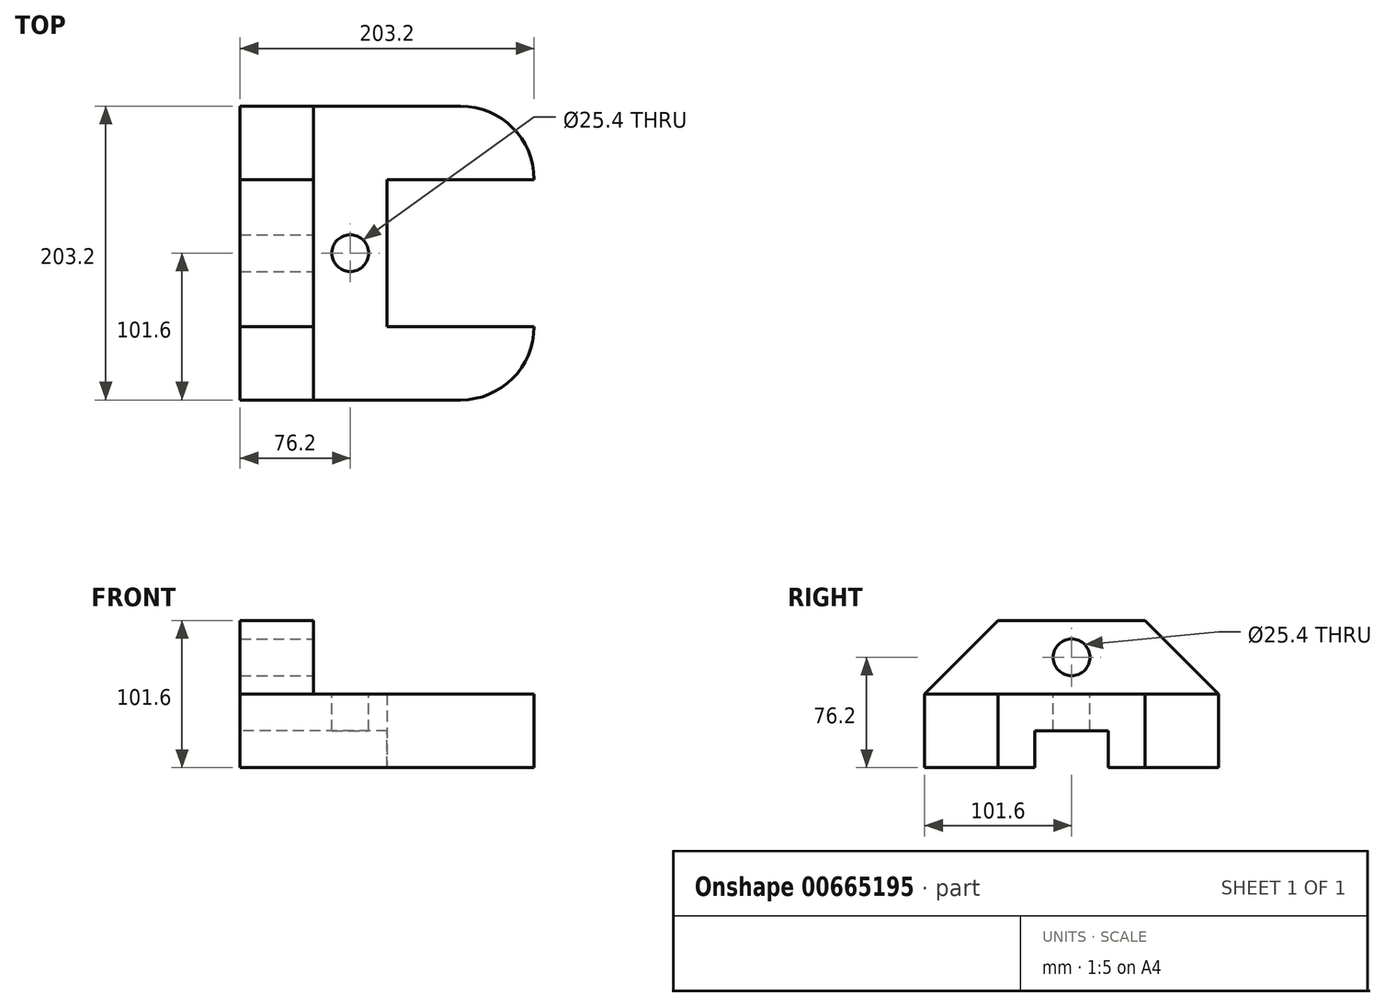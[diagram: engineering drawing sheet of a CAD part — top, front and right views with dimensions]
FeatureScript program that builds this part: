
annotation { "Feature Type Name" : "Feature", "Feature Type Description" : "" }
export const myFeature = defineFeature(function(context is Context, id is Id, definition is map)
    precondition{}
    {
        {
            var Q0;
            Q0=qCreatedBy(makeId("Front.planeOp"),FACE);
            var sketch = newSketch(context, id + "F0", { "sketchPlane" : qUnion([Q0])});
            skLineSegment(sketch, "E0", {"start": v(0, 0) * mm, "end": v(0, 76.2) * mm});
            skLineSegment(sketch, "E1", {"start": v(0, 76.2) * mm, "end": v(50.8, 76.2) * mm});
            skLineSegment(sketch, "E2", {"start": v(50.8, 76.2) * mm, "end": v(50.8, 25.4) * mm});
            skLineSegment(sketch, "E3", {"start": v(50.8, 25.4) * mm, "end": v(101.6, 25.4) * mm});
            skLineSegment(sketch, "E4", {"start": v(101.6, 25.4) * mm, "end": v(101.6, 0) * mm});
            skLineSegment(sketch, "E5", {"start": v(101.6, 0) * mm, "end": v(0, 0) * mm});
            skLineSegment(sketch, "E6", {"start": v(0, 0) * mm, "end": v(0, -25.4) * mm});
            skLineSegment(sketch, "E7", {"start": v(0, -25.4) * mm, "end": v(101.6, -25.4) * mm});
            skLineSegment(sketch, "E8", {"start": v(101.6, -25.4) * mm, "end": v(101.6, 0) * mm});
            skSolve(sketch);
        }
        {
            var Q0;
            Q0=makeQuery(id+"F0.imprint","IMPRINT",FACE,{"disambiguationData":[TD([[makeQuery(id+"F0.imprint","IMPRINT",EDGE,{"derivedFrom":sQuery(id+"F0.wireOp",EDGE,"E0")}),-1.0]])]});
            extrude(context, id + "F1", {"entities" : qUnion([Q0]), "endBound" : BoundingType.SYMMETRIC, "depth" : 101.6 * mm, "offsetDistance" : 25.4 * mm});
        }
        {
            var Q0;
            Q0=makeQuery(id+"F1.opExtrude","SWEPT_FACE",FACE,{"disambiguationData":[OSD([sQuery(id+"F0.wireOp",EDGE,"E5")])]});
            var sketch = newSketch(context, id + "F2", { "sketchPlane" : qUnion([Q0])});
            skLineSegment(sketch, "E9", {"start": v(101.6, 25.4) * mm, "end": v(0, 25.4) * mm});
            skLineSegment(sketch, "E10", {"start": v(101.6, -25.4) * mm, "end": v(0, -25.4) * mm});
            skSolve(sketch);
        }
        {
            var Q0;
            {var subQ0=sQuery(id+"F2.wireOp",EDGE,"E9");Q0=makeQuery(id+"F2.imprint","IMPRINT",FACE,{"disambiguationData":[TD([[makeQuery(id+"F2.imprint","IMPRINT",EDGE,{"derivedFrom":subQ0}),-1.0]])]});}
            var Q1;
            {var subQ0=sQuery(id+"F2.wireOp",EDGE,"E10");Q1=makeQuery(id+"F2.imprint","IMPRINT",FACE,{"disambiguationData":[TD([[makeQuery(id+"F2.imprint","IMPRINT",EDGE,{"derivedFrom":subQ0}),1.0]])]});}
            extrude(context, id + "F3", {"entities" : qUnion([Q0, Q1]), "operationType" : NewBodyOperationType.ADD, "depth" : 25.4 * mm, "offsetDistance" : 25.4 * mm});
        }
        {
            var Q0;
            {var subQ0=sQuery(id+"F0.wireOp",EDGE,"E5");var subQ1=sQuery(id+"F0.wireOp",EDGE,"E6");var subQ2=sQuery(id+"F0.wireOp",EDGE,"E0");var subQ3=makeQuery(id+"F1.opExtrude","SWEPT_EDGE",EDGE,{"disambiguationData":[OSD([subQ2,subQ0,subQ1])]});Q0=makeQuery(id+"F3.boolean.opBoolean","MERGE",FACE,{"derivedFrom":[makeQuery(id+"F1.opExtrude","SWEPT_FACE",FACE,{"disambiguationData":[OSD([subQ2])]}),makeQuery(id+"F3.opExtrude","SWEPT_FACE",FACE,{"disambiguationData":[OSD([subQ2,subQ0,subQ1]),TDD([makeQuery(id+"F2.imprint","IMPRINT",EDGE,{"disambiguationData":[TD([[makeQuery(id+"F2.imprint","INTERSECT",VERTEX,{"derivedFrom":[subQ3,makeQuery(id+"F1.opExtrude","CAP_EDGE",EDGE,{"disambiguationData":[OSD([subQ0])],"isStart":true})]}),1.0]])],"derivedFrom":subQ3})])]}),makeQuery(id+"F3.opExtrude","SWEPT_FACE",FACE,{"disambiguationData":[OSD([subQ2,subQ0,subQ1]),TDD([makeQuery(id+"F2.imprint","IMPRINT",EDGE,{"disambiguationData":[TD([[makeQuery(id+"F2.imprint","INTERSECT",VERTEX,{"derivedFrom":[subQ3,makeQuery(id+"F1.opExtrude","CAP_EDGE",EDGE,{"disambiguationData":[OSD([subQ0])],"isStart":false})]}),-1.0]])],"derivedFrom":subQ3})])]})]});}
            var sketch = newSketch(context, id + "F4", { "sketchPlane" : qUnion([Q0])});
            skLineSegment(sketch, "E11", {"start": v(-50.8, -25.4) * mm, "end": v(-101.6, -25.4) * mm});
            skLineSegment(sketch, "E12", {"start": v(-101.6, -25.4) * mm, "end": v(-101.6, 25.4) * mm});
            skLineSegment(sketch, "E13", {"start": v(-101.6, 25.4) * mm, "end": v(-50.8, 25.4) * mm});
            skLineSegment(sketch, "E14", {"start": v(50.8, -25.4) * mm, "end": v(101.6, -25.4) * mm});
            skLineSegment(sketch, "E15", {"start": v(101.6, -25.4) * mm, "end": v(101.6, 25.4) * mm});
            skLineSegment(sketch, "E16", {"start": v(101.6, 25.4) * mm, "end": v(50.8, 25.4) * mm});
            skLineSegment(sketch, "E17", {"start": v(-50.8, 76.2) * mm, "end": v(-101.6, 25.4) * mm});
            skLineSegment(sketch, "E18", {"start": v(50.8, 76.2) * mm, "end": v(101.6, 25.4) * mm});
            skSolve(sketch);
        }
        {
            var Q0;
            {var subQ0=sQuery(id+"F4.wireOp",EDGE,"E16");Q0=makeQuery(id+"F4.imprint","IMPRINT",FACE,{"disambiguationData":[TD([[makeQuery(id+"F4.imprint","IMPRINT",EDGE,{"derivedFrom":subQ0}),-1.0]])]});}
            var Q1;
            {var subQ0=sQuery(id+"F4.wireOp",EDGE,"E13");Q1=makeQuery(id+"F4.imprint","IMPRINT",FACE,{"disambiguationData":[TD([[makeQuery(id+"F4.imprint","IMPRINT",EDGE,{"derivedFrom":subQ0}),1.0]])]});}
            extrude(context, id + "F5", {"entities" : qUnion([Q0, Q1]), "operationType" : NewBodyOperationType.ADD, "oppositeDirection" : true, "depth" : 50.8 * mm, "offsetDistance" : 25.4 * mm});
        }
        {
            var Q0;
            {var subQ0=sQuery(id+"F4.wireOp",EDGE,"E11");Q0=makeQuery(id+"F4.imprint","IMPRINT",FACE,{"disambiguationData":[TD([[makeQuery(id+"F4.imprint","IMPRINT",EDGE,{"derivedFrom":subQ0}),-1.0]])]});}
            var Q1;
            {var subQ0=sQuery(id+"F4.wireOp",EDGE,"E14");Q1=makeQuery(id+"F4.imprint","IMPRINT",FACE,{"disambiguationData":[TD([[makeQuery(id+"F4.imprint","IMPRINT",EDGE,{"derivedFrom":subQ0}),1.0]])]});}
            extrude(context, id + "F6", {"entities" : qUnion([Q0, Q1]), "operationType" : NewBodyOperationType.ADD, "oppositeDirection" : true, "depth" : 203.2 * mm, "offsetDistance" : 25.4 * mm});
        }
        {
            var Q0;
            Q0=makeQuery(id+"F6.opExtrude","CAP_EDGE",EDGE,{"disambiguationData":[OSD([sQuery(id+"F4.wireOp",EDGE,"E15")])],"isStart":false});
            var Q1;
            Q1=makeQuery(id+"F6.opExtrude","CAP_EDGE",EDGE,{"disambiguationData":[OSD([sQuery(id+"F4.wireOp",EDGE,"E12")])],"isStart":false});
            fillet(context, id + "F7", {"entities" : qUnion([Q0, Q1]), "radius" : 50.8 * mm, "tangentPropagation" : true, "allowEdgeOverflow" : false});
        }
        {
            var Q0;
            Q0=makeQuery(id+"F6.boolean.opBoolean","MERGE",FACE,{"derivedFrom":[makeQuery(id+"F1.opExtrude","SWEPT_FACE",FACE,{"disambiguationData":[OSD([sQuery(id+"F0.wireOp",EDGE,"E3")])]}),makeQuery(id+"F6.opExtrude","SWEPT_FACE",FACE,{"disambiguationData":[OSD([sQuery(id+"F4.wireOp",EDGE,"E13")])]}),makeQuery(id+"F6.opExtrude","SWEPT_FACE",FACE,{"disambiguationData":[OSD([sQuery(id+"F4.wireOp",EDGE,"E16")])]})]});
            var sketch = newSketch(context, id + "F8", { "sketchPlane" : qUnion([Q0])});
            skPoint(sketch, "E19", {"position": v(76.2, 0) * mm});
            skSolve(sketch);
        }
        {
            var Q0;
            {var subQ0=sQuery(id+"F0.wireOp",EDGE,"E6");var subQ1=sQuery(id+"F0.wireOp",EDGE,"E5");var subQ2=sQuery(id+"F0.wireOp",EDGE,"E0");Q0=makeQuery(id+"F5.boolean.opBoolean","MERGE",FACE,{"derivedFrom":[makeQuery(id+"F1.opExtrude","SWEPT_FACE",FACE,{"disambiguationData":[OSD([sQuery(id+"F0.wireOp",EDGE,"E2")])]}),makeQuery(id+"F5.opExtrude","CAP_FACE",FACE,{"disambiguationData":[OSD([subQ2,subQ1,subQ0,sQuery(id+"F4.wireOp",EDGE,"E13"),sQuery(id+"F4.wireOp",EDGE,"E17")])],"isStart":false}),makeQuery(id+"F5.opExtrude","CAP_FACE",FACE,{"disambiguationData":[OSD([subQ2,subQ1,subQ0,sQuery(id+"F4.wireOp",EDGE,"E16"),sQuery(id+"F4.wireOp",EDGE,"E18")])],"isStart":false})]});}
            var sketch = newSketch(context, id + "F9", { "sketchPlane" : qUnion([Q0])});
            skPoint(sketch, "E20", {"position": v(0, 50.8) * mm});
            skSolve(sketch);
        }
        {
            var Q0;
            Q0=sQuery(id+"F9.wireOp",VERTEX,"E20");
            var Q1;
            Q1=sQuery(id+"F8.wireOp",VERTEX,"E19");
            var Q2;
            Q2=makeQuery(id+"F1.opExtrude","SWEPT_BODY",BODY,{"disambiguationData":[OSD([sQuery(id+"F0.wireOp",EDGE,"E0"),sQuery(id+"F0.wireOp",EDGE,"E1"),sQuery(id+"F0.wireOp",EDGE,"E2"),sQuery(id+"F0.wireOp",EDGE,"E3"),sQuery(id+"F0.wireOp",EDGE,"E4"),sQuery(id+"F0.wireOp",EDGE,"E5")])]});
            hole(context, id + "F10", {"style" : HoleStyle.SIMPLE, "endStyle" : HoleEndStyle.THROUGH, "holeDiameter" : 25.4 * mm, "majorDiameter" : 6.35 * mm, "isTappedThrough" : true, "tappedDepth" : 12.7 * mm, "tapClearance" : 3, "locations" : qUnion([Q0, Q1]), "scope" : qUnion([Q2])});
        }
    });
